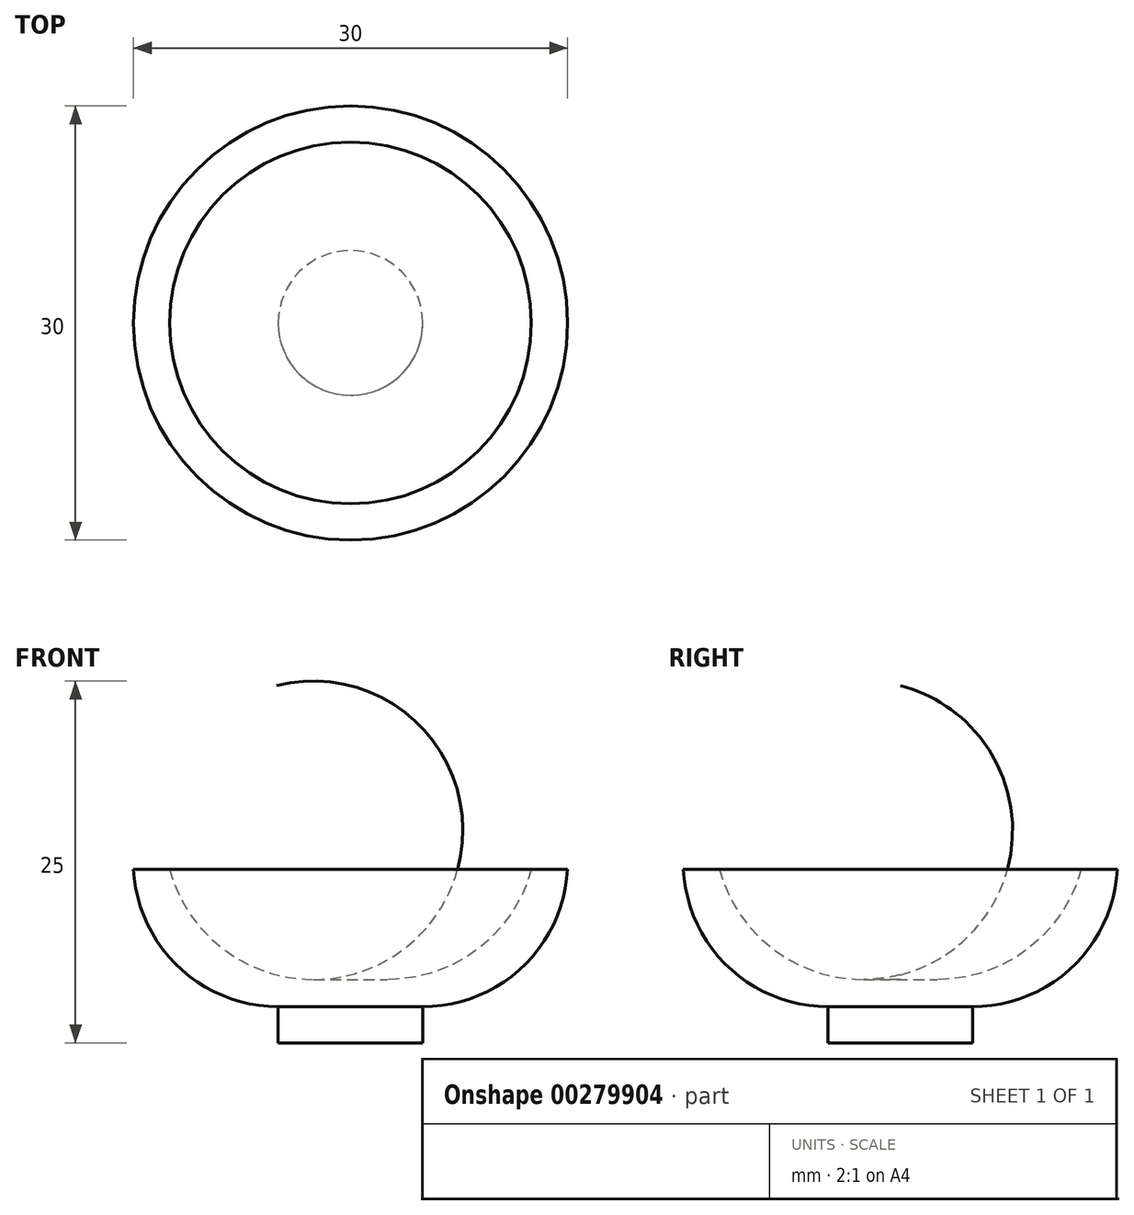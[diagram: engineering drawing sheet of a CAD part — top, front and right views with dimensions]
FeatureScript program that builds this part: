
annotation { "Feature Type Name" : "Feature", "Feature Type Description" : "" }
export const myFeature = defineFeature(function(context is Context, id is Id, definition is map)
    precondition{}
    {
        {
            var Q0;
            Q0=qCreatedBy(makeId("Top.planeOp"),FACE);
            var sketch = newSketch(context, id + "F0", { "sketchPlane" : qUnion([Q0])});
            skCircle(sketch, "E0", {"center": v(0, 0) * mm, "radius": 5 * mm});
            skSolve(sketch);
        }
        {
            var Q0;
            Q0=makeQuery(id+"F0.imprint","IMPRINT",FACE,{"disambiguationData":[TD([[makeQuery(id+"F0.imprint","IMPRINT",EDGE,{"derivedFrom":sQuery(id+"F0.wireOp",EDGE,"E0")}),1.0]])]});
            extrude(context, id + "F1", {"entities" : qUnion([Q0]), "depth" : 2.5 * mm});
        }
        {
            var Q0;
            Q0=qCreatedBy(makeId("Right.planeOp"),FACE);
            var sketch = newSketch(context, id + "F2", { "sketchPlane" : qUnion([Q0])});
            skLineSegment(sketch, "E1", {"start": v(0, 0) * mm, "end": v(0, 12) * mm});
            skLineSegment(sketch, "E2", {"start": v(0, 12) * mm, "end": v(15, 12) * mm});
            skLineSegment(sketch, "E3", {"start": v(15, 12) * mm, "end": v(-15, 12) * mm});
            skLineSegment(sketch, "E4", {"start": v(0, 0) * mm, "end": v(0, 2.5) * mm});
            skLineSegment(sketch, "E5", {"start": v(0, 2.5) * mm, "end": v(5, 2.5) * mm});
            skArc(sketch, "E6", {"start": v(5, 2.5) * mm, "mid": v(11.9, 5.25) * mm, "end": v(15, 12) * mm});
            skLineSegment(sketch, "E7", {"start": v(15, 12) * mm, "end": v(12.5, 12) * mm});
            skLineSegment(sketch, "E8", {"start": v(0, 2.5) * mm, "end": v(0, 4.7) * mm});
            skArc(sketch, "E9", {"start": v(0, 4.7) * mm, "mid": v(7.75, 5.79) * mm, "end": v(12.5, 12) * mm});
            skSolve(sketch);
        }
        {
            var Q0;
            Q0=makeQuery(id+"F2.imprint","IMPRINT",FACE,{"disambiguationData":[TD([[makeQuery(id+"F2.imprint","IMPRINT",EDGE,{"derivedFrom":sQuery(id+"F2.wireOp",EDGE,"E5")}),1.0]])]});
            var Q1;
            Q1=sQuery(id+"F2.wireOp",EDGE,"E1");
            revolve(context, id + "F3", {"operationType" : NewBodyOperationType.ADD, "entities" : qUnion([Q0]), "axis" : qUnion([Q1]), "revolveType" : RevolveType.FULL});
        }
    });
